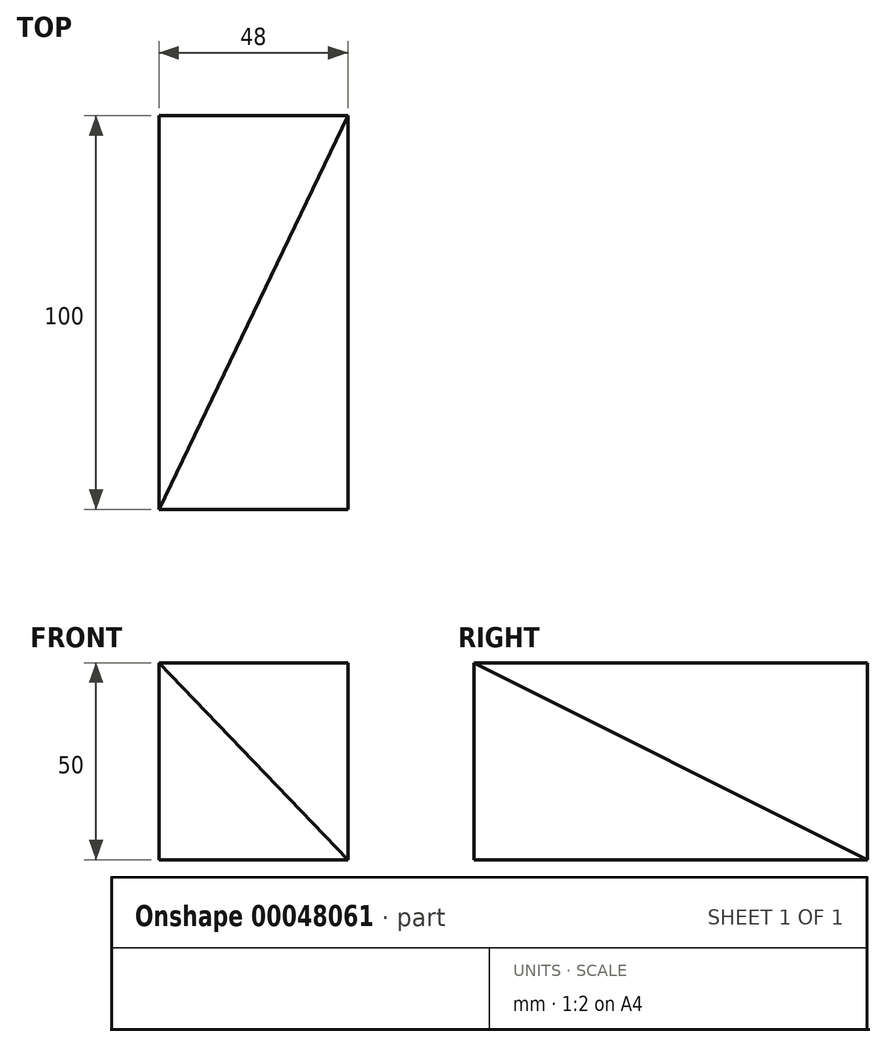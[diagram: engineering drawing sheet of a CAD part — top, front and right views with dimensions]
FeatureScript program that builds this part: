
annotation { "Feature Type Name" : "Feature", "Feature Type Description" : "" }
export const myFeature = defineFeature(function(context is Context, id is Id, definition is map)
    precondition{}
    {
        {
            var Q0;
            Q0=qCreatedBy(makeId("Front.planeOp"),FACE);
            var sketch = newSketch(context, id + "F0", { "sketchPlane" : qUnion([Q0])});
            skLineSegment(sketch, "E0.bottom", {"start": v(0, 0) * mm, "end": v(48, 0) * mm});
            skLineSegment(sketch, "E0.top", {"start": v(0, 50) * mm, "end": v(48, 50) * mm});
            skLineSegment(sketch, "E0.left", {"start": v(0, 0) * mm, "end": v(0, 50) * mm});
            skLineSegment(sketch, "E0.right", {"start": v(48, 0) * mm, "end": v(48, 50) * mm});
            skLineSegment(sketch, "E1", {"start": v(0, 50) * mm, "end": v(48, 0) * mm});
            skSolve(sketch);
        }
        {
            var Q0;
            Q0=makeQuery(id+"F0.imprint","IMPRINT",FACE,{"disambiguationData":[TD([[makeQuery(id+"F0.imprint","IMPRINT",EDGE,{"derivedFrom":sQuery(id+"F0.wireOp",EDGE,"E0.bottom")}),1.0]])]});
            extrude(context, id + "F1", {"entities" : qUnion([Q0]), "depth" : 100 * mm});
        }
        {
            var Q1;
            Q1=makeQuery(id+"F0.imprint","IMPRINT",FACE,{"disambiguationData":[TD([[makeQuery(id+"F0.imprint","IMPRINT",EDGE,{"derivedFrom":sQuery(id+"F0.wireOp",EDGE,"E0.top")}),-1.0]])]});
            var Q2;
            Q2=makeQuery(id+"F1.opExtrude","CAP_VERTEX",VERTEX,{"disambiguationData":[OSD([sQuery(id+"F0.wireOp",EDGE,"E0.top"),sQuery(id+"F0.wireOp",EDGE,"E0.left"),sQuery(id+"F0.wireOp",EDGE,"E1")])],"isStart":false});
            loft(context, id + "F2", {"operationType" : NewBodyOperationType.ADD, "sheetProfilesArray" : [{ "sheetProfileEntities" : qUnion([Q1]) }, { "sheetProfileEntities" : qUnion([Q2]) }]});
        }
    });
